# Revit family: Шаровой кран
name_source: partatom
category: Арматура трубопроводов
revit_build: Autodesk Revit 2017 (Build: 20171027_0315(x64)
units: mm (PartAtom-declared; Revit-internal decimal feet)

## family parameters
Всегда вертикально = Да
На основе рабочей плоскости = Нет
Общий = Нет
При загрузке вырезать с полостями = Нет
Размер круглого соединителя = Использовать радиус
Тип детали = Вставляется

## types (6) — shared parameters
ADSK_Единица измерения = шт
ADSK_Завод-изготовитель = Itap
ADSK_Наименование = Кран шаровой
URL = http://www.itap.it
Группа модели = Кран шаровой
Изготовитель = Itap
Материал полимера = Фильтр_Черный
Материал стальной части = Фильтр_Латунь
Материал фитинга = РВК_Полипропилен PPR
Разработчик = ООО ПРОРУБИМ
Разработчик (телефон) = +7(495)649-85-43
Разработчик модели (URL) = http://prorubim.com
zero-valued in all types: ADSK_Масса

## per-type parameters (varying)
| type | A | A1 | ADSK_Код изделия | B | C | D | DN | E | E+t | F | G | R | x | Переключатель УГО |
| DN50 | 151 мм | 60 мм |  | 84 мм | 96 мм | 158 мм | 50 мм | 50 мм | 54 мм | 21 мм | 17 мм | 25 мм | 110 мм | Нет |
| DN40 | 132 мм | 53 мм |  | 70 мм | 81 мм | 138 мм | 40 мм | 39 мм | 43 мм | 18 мм | 16 мм | 20 мм | 95 мм | Нет |
| DN32 | 115 мм | 46 мм | 26753 | 57 мм | 64 мм | 70 мм | 32 мм | 32 мм | 36 мм | 17 мм | 17 мм | 16 мм | 81 мм | Нет |
| DN25 | 99 мм | 40 мм | 26098 | 46 мм | 52 мм | 62 мм | 25 мм | 25 мм | 29 мм | 15 мм | 16 мм | 13 мм | 68 мм | Нет |
| DN20 | 86 мм | 34 мм | 26097 | 37 мм | 47 мм | 62 мм | 20 мм | 20 мм | 24 мм | 14 мм | 14 мм | 10 мм | 57 мм | Нет |
| DN15 | 74 мм | 30 мм |  | 31 мм | 41 мм | 47 мм | 15 мм | 15 мм | 19 мм | 13 мм | 12 мм | 8 мм | 47 мм | Да |

note: column(s) folded — value = type name in every type: ADSK_Обозначение
